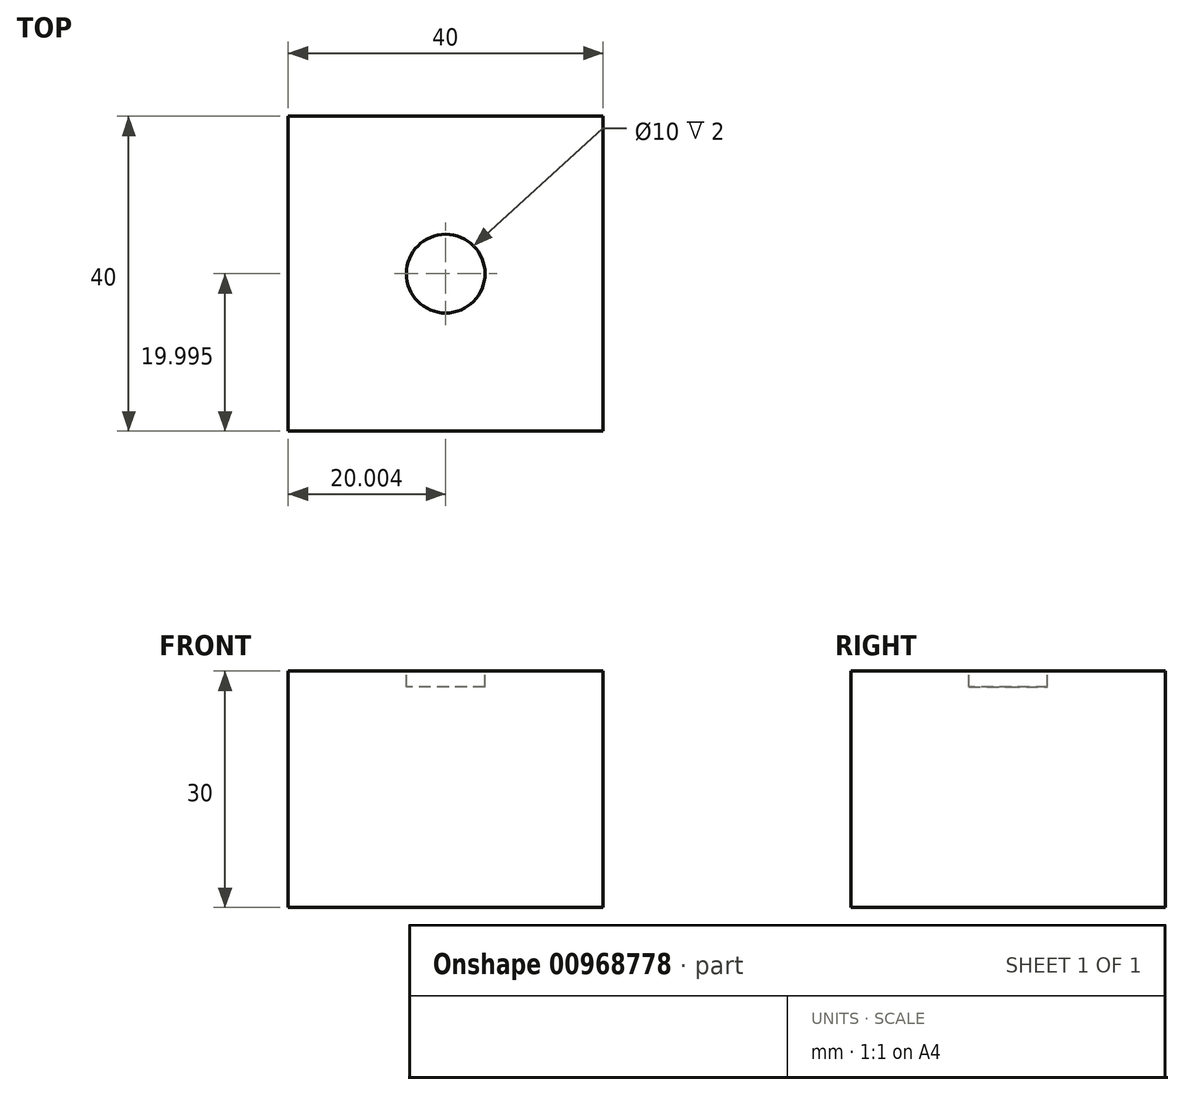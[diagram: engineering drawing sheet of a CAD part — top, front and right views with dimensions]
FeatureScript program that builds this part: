
annotation { "Feature Type Name" : "Feature", "Feature Type Description" : "" }
export const myFeature = defineFeature(function(context is Context, id is Id, definition is map)
    precondition{}
    {
        {
            var Q0;
            Q0=qCreatedBy(makeId("Top.planeOp"),FACE);
            var sketch = newSketch(context, id + "F0", { "sketchPlane" : qUnion([Q0])});
            skLineSegment(sketch, "E0.bottom", {"start": v(-99.96, 51.64) * mm, "end": v(-59.96, 51.64) * mm});
            skLineSegment(sketch, "E0.top", {"start": v(-99.96, 11.64) * mm, "end": v(-59.96, 11.64) * mm});
            skLineSegment(sketch, "E0.left", {"start": v(-99.96, 51.64) * mm, "end": v(-99.96, 11.64) * mm});
            skLineSegment(sketch, "E0.right", {"start": v(-59.96, 51.64) * mm, "end": v(-59.96, 11.64) * mm});
            skSolve(sketch);
        }
        {
            var Q0;
            Q0=makeQuery(id+"F0.imprint","IMPRINT",FACE,{"disambiguationData":[TD([[makeQuery(id+"F0.imprint","IMPRINT",EDGE,{"derivedFrom":sQuery(id+"F0.wireOp",EDGE,"E0.bottom")}),-1.0]])]});
            extrude(context, id + "F1", {"entities" : qUnion([Q0]), "depth" : 30 * mm, "offsetDistance" : 25 * mm});
        }
        {
            var Q0;
            Q0=makeQuery(id+"F1.opExtrude","CAP_FACE",FACE,{"disambiguationData":[OSD([sQuery(id+"F0.wireOp",EDGE,"E0.bottom"),sQuery(id+"F0.wireOp",EDGE,"E0.top"),sQuery(id+"F0.wireOp",EDGE,"E0.left"),sQuery(id+"F0.wireOp",EDGE,"E0.right")])],"isStart":false});
            var sketch = newSketch(context, id + "F2", { "sketchPlane" : qUnion([Q0])});
            skCircle(sketch, "E1", {"center": v(-79.96, 31.64) * mm, "radius": 5 * mm});
            skPoint(sketch, "E1.centerSnap0", {"position": v(-59.96, 31.64) * mm});
            skPoint(sketch, "E1.centerSnap1", {"position": v(-79.96, 51.64) * mm});
            skSolve(sketch);
        }
        {
            var Q0;
            Q0 = qSketchRegion(id + "F2", true);
            extrude(context, id + "F3", {"entities" : qUnion([Q0]), "operationType" : NewBodyOperationType.REMOVE, "oppositeDirection" : true, "depth" : 2 * mm, "offsetDistance" : 25 * mm});
        }
    });
